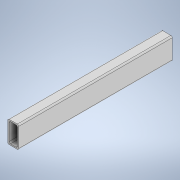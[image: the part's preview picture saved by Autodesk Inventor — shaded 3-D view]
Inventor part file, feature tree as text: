
AUTODESK INVENTOR PART (.ipt)
format: ipt  version: 2020 (Build 240168000, 168)  size: 126,464 bytes
history: native  units: in
note: dims shown in document units (in); Inventor stores cm internally (conversion verified against a paired STEP export)
features: extrude x1, sketch x1
ambient origin geometry x8: Origin, YZ Plane, XZ Plane, XY Plane, X Axis, Y Axis, Z Axis, Center Point
bodies: Solid1 (feature_tree)
feature tree (2):
  extrude  "Extrusion1"  Depth=1.0in
  sketch  "Sketch1"  dims[d0=2.0in d1=1.0in d2=0.125in d3=0.125in d4=0.125in d5=0.125in d6=0.125in d7=0.125in d8=0.125in d9=0.125in d10=0.125in d11=14.0in d12=0.0in]
